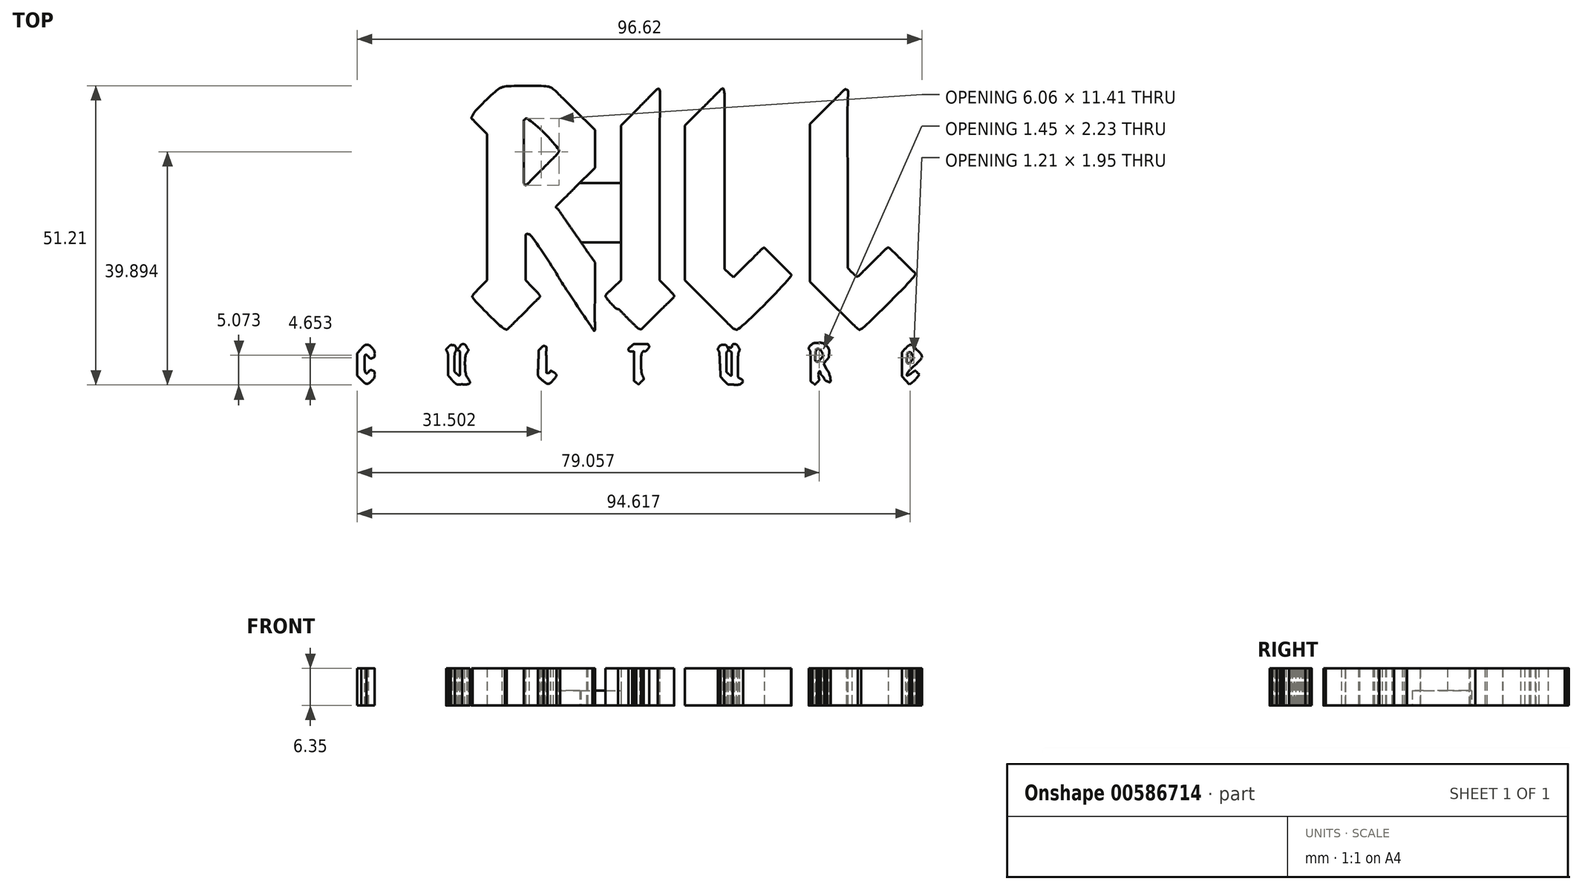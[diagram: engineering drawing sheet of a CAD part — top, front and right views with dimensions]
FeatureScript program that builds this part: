
annotation { "Feature Type Name" : "Feature", "Feature Type Description" : "" }
export const myFeature = defineFeature(function(context is Context, id is Id, definition is map)
    precondition{}
    {
        {
            var Q0;
            Q0=qCreatedBy(makeId("Top.planeOp"),FACE);
            var sketch = newSketch(context, id + "F0", { "sketchPlane" : qUnion([Q0])});
            skFitSpline(sketch, "E0", {"points": [v(-13.18, -32.43) * mm, v(-13.35, -32.29) * mm, v(-13.68, -31.93) * mm, v(-13.92, -31.65) * mm]});
            skFitSpline(sketch, "E1", {"points": [v(-13.92, -31.65) * mm, v(-14.33, -31.16) * mm, v(-14.34, -31.08) * mm, v(-14.34, -29.31) * mm]});
            skFitSpline(sketch, "E2", {"points": [v(-14.34, -29.31) * mm, v(-14.34, -28.25) * mm, v(-14.41, -27.32) * mm, v(-14.52, -27.09) * mm]});
            skFitSpline(sketch, "E3", {"points": [v(-14.52, -27.09) * mm, v(-14.68, -26.75) * mm, v(-14.65, -26.64) * mm, v(-14.33, -26.3) * mm]});
            skFitSpline(sketch, "E4", {"points": [v(-14.33, -26.3) * mm, v(-14.12, -26.08) * mm, v(-13.83, -25.93) * mm, v(-13.66, -25.96) * mm]});
            skFitSpline(sketch, "E5", {"points": [v(-13.66, -25.96) * mm, v(-13.23, -26.02) * mm, v(-12.94, -26.64) * mm, v(-13.12, -27.12) * mm]});
            skFitSpline(sketch, "E6", {"points": [v(-13.12, -27.12) * mm, v(-13.2, -27.32) * mm, v(-13.26, -28.16) * mm, v(-13.26, -29) * mm]});
            skFitSpline(sketch, "E7", {"points": [v(-13.26, -29) * mm, v(-13.26, -30.36) * mm, v(-13.23, -30.52) * mm, v(-12.9, -30.83) * mm]});
            skFitSpline(sketch, "E8", {"points": [v(-12.9, -30.83) * mm, v(-12.7, -31.01) * mm, v(-12.5, -31.16) * mm, v(-12.44, -31.16) * mm]});
            skFitSpline(sketch, "E9", {"points": [v(-12.44, -31.16) * mm, v(-12.39, -31.16) * mm, v(-12.34, -30.23) * mm, v(-12.34, -29.1) * mm]});
            skFitSpline(sketch, "E10", {"points": [v(-12.34, -29.1) * mm, v(-12.34, -27.4) * mm, v(-12.38, -27) * mm, v(-12.57, -26.89) * mm]});
            skFitSpline(sketch, "E11", {"points": [v(-12.57, -26.89) * mm, v(-12.78, -26.77) * mm, v(-12.76, -26.7) * mm, v(-12.45, -26.34) * mm]});
            skFitSpline(sketch, "E12", {"points": [v(-12.45, -26.34) * mm, v(-12, -25.81) * mm, v(-11.55, -25.81) * mm, v(-11.16, -26.35) * mm]});
            skFitSpline(sketch, "E13", {"points": [v(-11.16, -26.35) * mm, v(-10.9, -26.72) * mm, v(-10.88, -26.82) * mm, v(-11.06, -27.16) * mm]});
            skFitSpline(sketch, "E14", {"points": [v(-11.06, -27.16) * mm, v(-11.37, -27.76) * mm, v(-11.33, -30.9) * mm, v(-11, -31.58) * mm]});
            skFitSpline(sketch, "E15", {"points": [v(-11, -31.58) * mm, v(-10.63, -32.38) * mm, v(-10.84, -32.62) * mm, v(-11.97, -32.66) * mm]});
            skFitSpline(sketch, "E16", {"points": [v(-11.97, -32.66) * mm, v(-12.65, -32.7) * mm, v(-12.95, -32.63) * mm, v(-13.18, -32.43) * mm]});
            skFitSpline(sketch, "E17", {"points": [v(17.85, -32.4) * mm, v(17.47, -32.1) * mm, v(17.46, -32.1) * mm, v(17.46, -29.6) * mm]});
            skFitSpline(sketch, "E18", {"points": [v(17.46, -29.6) * mm, v(17.46, -27.09) * mm, v(17.46, -27.08) * mm, v(17.1, -27.03) * mm]});
            skFitSpline(sketch, "E19", {"points": [v(17.1, -27.03) * mm, v(16.58, -26.96) * mm, v(16.53, -26.59) * mm, v(17, -26.15) * mm]});
            skFitSpline(sketch, "E20", {"points": [v(17, -26.15) * mm, v(17.36, -25.81) * mm, v(17.54, -25.77) * mm, v(18.63, -25.77) * mm]});
            skFitSpline(sketch, "E21", {"points": [v(18.63, -25.77) * mm, v(19.58, -25.77) * mm, v(19.88, -25.83) * mm, v(19.95, -26) * mm]});
            skFitSpline(sketch, "E22", {"points": [v(19.95, -26) * mm, v(20.04, -26.25) * mm, v(19.43, -27) * mm, v(19.14, -27) * mm]});
            skFitSpline(sketch, "E23", {"points": [v(19.14, -27) * mm, v(19.04, -27) * mm, v(18.92, -27.11) * mm, v(18.87, -27.25) * mm]});
            skFitSpline(sketch, "E24", {"points": [v(18.87, -27.25) * mm, v(18.7, -27.69) * mm, v(18.77, -30.74) * mm, v(18.96, -31.27) * mm]});
            skFitSpline(sketch, "E25", {"points": [v(18.96, -31.27) * mm, v(19.13, -31.75) * mm, v(19.12, -31.82) * mm, v(18.69, -32.24) * mm]});
            skFitSpline(sketch, "E26", {"points": [v(18.69, -32.24) * mm, v(18.23, -32.7) * mm, v(18.23, -32.7) * mm, v(17.85, -32.4) * mm]});
            skLineSegment(sketch, "E27", {"start": v(-13.18, -32.43) * mm, "end": v(-13.18, -32.43) * mm});
            skFitSpline(sketch, "E28", {"points": [v(32.16, -29.32) * mm, v(32.11, -28.17) * mm, v(32.02, -27.11) * mm, v(31.95, -26.96) * mm]});
            skFitSpline(sketch, "E29", {"points": [v(31.95, -26.96) * mm, v(31.8, -26.63) * mm, v(32.38, -25.93) * mm, v(32.8, -25.93) * mm]});
            skFitSpline(sketch, "E30", {"points": [v(32.8, -25.93) * mm, v(33.14, -25.93) * mm, v(33.57, -26.74) * mm, v(33.39, -27.03) * mm]});
            skFitSpline(sketch, "E31", {"points": [v(33.39, -27.03) * mm, v(33.31, -27.14) * mm, v(33.25, -27.98) * mm, v(33.25, -28.89) * mm]});
            skFitSpline(sketch, "E32", {"points": [v(33.25, -28.89) * mm, v(33.25, -30.39) * mm, v(33.28, -30.56) * mm, v(33.59, -30.85) * mm]});
            skFitSpline(sketch, "E33", {"points": [v(33.59, -30.85) * mm, v(33.77, -31.02) * mm, v(33.98, -31.16) * mm, v(34.05, -31.16) * mm]});
            skFitSpline(sketch, "E34", {"points": [v(34.05, -31.16) * mm, v(34.12, -31.16) * mm, v(34.17, -30.27) * mm, v(34.17, -29.18) * mm]});
            skFitSpline(sketch, "E35", {"points": [v(34.17, -29.18) * mm, v(34.17, -27.6) * mm, v(34.13, -27.16) * mm, v(33.94, -27) * mm]});
            skFitSpline(sketch, "E36", {"points": [v(33.94, -27) * mm, v(33.65, -26.76) * mm, v(33.64, -26.39) * mm, v(33.93, -26.39) * mm]});
            skFitSpline(sketch, "E37", {"points": [v(33.93, -26.39) * mm, v(34.05, -26.39) * mm, v(34.18, -26.28) * mm, v(34.23, -26.16) * mm]});
            skFitSpline(sketch, "E38", {"points": [v(34.23, -26.16) * mm, v(34.37, -25.8) * mm, v(35.03, -25.88) * mm, v(35.31, -26.3) * mm]});
            skFitSpline(sketch, "E39", {"points": [v(35.31, -26.3) * mm, v(35.5, -26.6) * mm, v(35.52, -26.78) * mm, v(35.4, -27.08) * mm]});
            skFitSpline(sketch, "E40", {"points": [v(35.4, -27.08) * mm, v(35.32, -27.3) * mm, v(35.25, -28.38) * mm, v(35.25, -29.46) * mm]});
            skFitSpline(sketch, "E41", {"points": [v(35.25, -29.46) * mm, v(35.25, -31.03) * mm, v(35.3, -31.47) * mm, v(35.48, -31.63) * mm]});
            skFitSpline(sketch, "E42", {"points": [v(35.48, -31.63) * mm, v(36.1, -32.13) * mm, v(35.46, -32.7) * mm, v(34.32, -32.7) * mm]});
            skFitSpline(sketch, "E43", {"points": [v(34.32, -32.7) * mm, v(33.55, -32.68) * mm, v(33.43, -32.63) * mm, v(32.87, -32.04) * mm]});
            skLineSegment(sketch, "E44", {"start": v(32.87, -32.04) * mm, "end": v(32.25, -31.4) * mm});
            skLineSegment(sketch, "E45", {"start": v(32.25, -31.4) * mm, "end": v(32.16, -29.32) * mm});
            skFitSpline(sketch, "E46", {"points": [v(48.02, -32.41) * mm, v(47.66, -32.12) * mm, v(47.65, -32.07) * mm, v(47.65, -29.6) * mm]});
            skFitSpline(sketch, "E47", {"points": [v(47.65, -29.6) * mm, v(47.65, -28.21) * mm, v(47.6, -26.96) * mm, v(47.52, -26.81) * mm]});
            skFitSpline(sketch, "E48", {"points": [v(47.52, -26.81) * mm, v(47.35, -26.46) * mm, v(48.22, -25.62) * mm, v(48.75, -25.62) * mm]});
            skFitSpline(sketch, "E49", {"points": [v(48.75, -25.62) * mm, v(49.68, -25.62) * mm, v(50.8, -26.67) * mm, v(50.8, -27.55) * mm]});
            skFitSpline(sketch, "E50", {"points": [v(50.8, -27.55) * mm, v(50.8, -27.91) * mm, v(50.67, -28.24) * mm, v(50.35, -28.6) * mm]});
            skFitSpline(sketch, "E51", {"points": [v(50.35, -29.99) * mm, v(50.92, -31.07) * mm, v(51, -32.26) * mm, v(50.5, -32.13) * mm]});
            skFitSpline(sketch, "E52", {"points": [v(50.5, -32.13) * mm, v(50.32, -32.09) * mm, v(50.1, -31.9) * mm, v(50, -31.72) * mm]});
            skFitSpline(sketch, "E53", {"points": [v(50, -31.72) * mm, v(49.91, -31.55) * mm, v(49.75, -31.31) * mm, v(49.64, -31.2) * mm]});
            skFitSpline(sketch, "E54", {"points": [v(49.64, -31.2) * mm, v(49.54, -31.1) * mm, v(49.42, -30.93) * mm, v(49.39, -30.83) * mm]});
            skFitSpline(sketch, "E55", {"points": [v(49.39, -30.83) * mm, v(49.25, -30.41) * mm, v(49, -30.9) * mm, v(49.07, -31.43) * mm]});
            skFitSpline(sketch, "E56", {"points": [v(49.07, -31.43) * mm, v(49.13, -31.9) * mm, v(49.07, -32.07) * mm, v(48.77, -32.36) * mm]});
            skFitSpline(sketch, "E57", {"points": [v(48.77, -32.36) * mm, v(48.4, -32.71) * mm, v(48.39, -32.71) * mm, v(48.02, -32.41) * mm]});
            skLineSegment(sketch, "E58", {"start": v(50.35, -28.6) * mm, "end": v(49.89, -29.12) * mm});
            skLineSegment(sketch, "E59", {"start": v(49.89, -29.12) * mm, "end": v(50.35, -29.99) * mm});
            skFitSpline(sketch, "E60", {"points": [v(49.51, -28.16) * mm, v(49.87, -27.8) * mm, v(49.88, -27.75) * mm, v(49.66, -27.33) * mm]});
            skFitSpline(sketch, "E61", {"points": [v(49.66, -27.33) * mm, v(49.41, -26.85) * mm, v(48.81, -26.6) * mm, v(48.62, -26.9) * mm]});
            skFitSpline(sketch, "E62", {"points": [v(48.62, -26.9) * mm, v(48.56, -27) * mm, v(48.5, -27.3) * mm, v(48.5, -27.57) * mm]});
            skFitSpline(sketch, "E63", {"points": [v(48.5, -27.57) * mm, v(48.5, -28.6) * mm, v(48.85, -28.82) * mm, v(49.51, -28.16) * mm]});
            skFitSpline(sketch, "E64", {"points": [v(63.9, -26.56) * mm, v(64.24, -26.21) * mm, v(64.65, -25.93) * mm, v(64.81, -25.93) * mm]});
            skFitSpline(sketch, "E65", {"points": [v(64.81, -25.93) * mm, v(64.97, -25.93) * mm, v(65.39, -26.26) * mm, v(65.73, -26.66) * mm]});
            skFitSpline(sketch, "E66", {"points": [v(65.73, -26.66) * mm, v(66.67, -27.75) * mm, v(66.62, -28.23) * mm, v(65.44, -29.47) * mm]});
            skFitSpline(sketch, "E67", {"points": [v(65.44, -29.47) * mm, v(64.3, -30.67) * mm, v(64.17, -31.17) * mm, v(65.15, -30.6) * mm]});
            skFitSpline(sketch, "E68", {"points": [v(65.15, -30.6) * mm, v(65.58, -30.34) * mm, v(65.6, -30.34) * mm, v(65.93, -30.66) * mm]});
            skLineSegment(sketch, "E69", {"start": v(63.92, -32.01) * mm, "end": v(63.28, -31.32) * mm});
            skLineSegment(sketch, "E70", {"start": v(63.28, -31.32) * mm, "end": v(63.28, -29.26) * mm});
            skLineSegment(sketch, "E71", {"start": v(63.28, -29.26) * mm, "end": v(63.28, -27.2) * mm});
            skLineSegment(sketch, "E72", {"start": v(63.28, -27.2) * mm, "end": v(63.9, -26.56) * mm});
            skLineSegment(sketch, "E73", {"start": v(63.9, -26.56) * mm, "end": v(63.92, -32.01) * mm});
            skFitSpline(sketch, "E74", {"points": [v(65.85, -31.53) * mm, v(65.62, -31.82) * mm, v(65.24, -32.2) * mm, v(65, -32.38) * mm]});
            skLineSegment(sketch, "E75", {"start": v(65.93, -30.66) * mm, "end": v(66.26, -31) * mm});
            skLineSegment(sketch, "E76", {"start": v(66.26, -31) * mm, "end": v(65.85, -31.53) * mm});
            skFitSpline(sketch, "E77", {"points": [v(65, -28.52) * mm, v(65.3, -28.21) * mm, v(65.32, -28.15) * mm, v(65.11, -27.79) * mm]});
            skFitSpline(sketch, "E78", {"points": [v(65.11, -27.79) * mm, v(64.78, -27.2) * mm, v(64.3, -27.26) * mm, v(64.24, -27.9) * mm]});
            skFitSpline(sketch, "E79", {"points": [v(64.24, -27.9) * mm, v(64.14, -28.87) * mm, v(64.42, -29.1) * mm, v(65, -28.52) * mm]});
            skLineSegment(sketch, "E80", {"start": v(65, -32.38) * mm, "end": v(64.55, -32.7) * mm});
            skLineSegment(sketch, "E81", {"start": v(64.55, -32.7) * mm, "end": v(63.92, -32.01) * mm});
            skFitSpline(sketch, "E82", {"points": [v(-29.27, -26.64) * mm, v(-28.92, -26.25) * mm, v(-28.52, -25.93) * mm, v(-28.37, -25.93) * mm]});
            skFitSpline(sketch, "E83", {"points": [v(-28.37, -25.93) * mm, v(-27.97, -25.93) * mm, v(-26.97, -27) * mm, v(-26.97, -27.42) * mm]});
            skFitSpline(sketch, "E84", {"points": [v(-26.97, -27.42) * mm, v(-26.97, -27.94) * mm, v(-27.63, -28.23) * mm, v(-28.02, -27.88) * mm]});
            skFitSpline(sketch, "E85", {"points": [v(-28.02, -27.88) * mm, v(-28.18, -27.74) * mm, v(-28.35, -27.62) * mm, v(-28.4, -27.62) * mm]});
            skFitSpline(sketch, "E86", {"points": [v(-28.4, -27.62) * mm, v(-28.54, -27.62) * mm, v(-28.54, -30.62) * mm, v(-28.4, -30.75) * mm]});
            skFitSpline(sketch, "E87", {"points": [v(-28.4, -30.75) * mm, v(-28.35, -30.8) * mm, v(-28.18, -30.74) * mm, v(-28.02, -30.6) * mm]});
            skFitSpline(sketch, "E88", {"points": [v(-28.02, -30.6) * mm, v(-27.63, -30.25) * mm, v(-26.97, -30.54) * mm, v(-26.97, -31.05) * mm]});
            skFitSpline(sketch, "E89", {"points": [v(-26.97, -31.05) * mm, v(-26.97, -31.44) * mm, v(-28, -32.55) * mm, v(-28.35, -32.55) * mm]});
            skFitSpline(sketch, "E90", {"points": [v(-28.35, -32.55) * mm, v(-28.47, -32.55) * mm, v(-28.86, -32.24) * mm, v(-29.23, -31.85) * mm]});
            skLineSegment(sketch, "E91", {"start": v(-29.23, -31.85) * mm, "end": v(-29.9, -31.16) * mm});
            skLineSegment(sketch, "E92", {"start": v(-29.9, -31.16) * mm, "end": v(-29.9, -29.26) * mm});
            skLineSegment(sketch, "E93", {"start": v(-29.9, -29.26) * mm, "end": v(-29.9, -27.36) * mm});
            skLineSegment(sketch, "E94", {"start": v(-29.9, -27.36) * mm, "end": v(-29.27, -26.64) * mm});
            skFitSpline(sketch, "E95", {"points": [v(1.93, -32.09) * mm, v(1.13, -31.39) * mm, v(1.03, -30.98) * mm, v(1.09, -28.8) * mm]});
            skFitSpline(sketch, "E96", {"points": [v(1.09, -28.8) * mm, v(1.14, -26.93) * mm, v(1.15, -26.84) * mm, v(1.55, -26.45) * mm]});
            skFitSpline(sketch, "E97", {"points": [v(1.55, -26.45) * mm, v(1.8, -26.2) * mm, v(2.05, -26.07) * mm, v(2.2, -26.13) * mm]});
            skFitSpline(sketch, "E98", {"points": [v(2.2, -26.13) * mm, v(2.41, -26.21) * mm, v(2.45, -26.56) * mm, v(2.45, -28.46) * mm]});
            skFitSpline(sketch, "E99", {"points": [v(2.45, -28.46) * mm, v(2.45, -30.57) * mm, v(2.47, -30.7) * mm, v(2.74, -30.7) * mm]});
            skFitSpline(sketch, "E100", {"points": [v(2.74, -30.7) * mm, v(2.9, -30.7) * mm, v(3.07, -30.61) * mm, v(3.1, -30.5) * mm]});
            skFitSpline(sketch, "E101", {"points": [v(3.1, -30.5) * mm, v(3.16, -30.36) * mm, v(3.28, -30.37) * mm, v(3.6, -30.55) * mm]});
            skFitSpline(sketch, "E102", {"points": [v(3.6, -30.55) * mm, v(3.85, -30.67) * mm, v(4.07, -30.86) * mm, v(4.1, -30.96) * mm]});
            skFitSpline(sketch, "E103", {"points": [v(4.1, -30.96) * mm, v(4.18, -31.2) * mm, v(2.95, -32.55) * mm, v(2.66, -32.55) * mm]});
            skFitSpline(sketch, "E104", {"points": [v(2.66, -32.55) * mm, v(2.55, -32.55) * mm, v(2.22, -32.34) * mm, v(1.93, -32.09) * mm]});
            skLineSegment(sketch, "E105", {"start": v(-29.23, -31.85) * mm, "end": v(-29.23, -31.85) * mm});
            skFitSpline(sketch, "E106", {"points": [v(-28.7, -17.2) * mm, v(-28.52, -16.96) * mm, v(-27.75, -16.16) * mm, v(-26.98, -15.41) * mm]});
            skFitSpline(sketch, "E107", {"points": [v(-26.98, -15.41) * mm, v(-26.22, -14.67) * mm, v(-25.55, -13.9) * mm, v(-25.5, -13.72) * mm]});
            skFitSpline(sketch, "E108", {"points": [v(-25.5, -13.72) * mm, v(-25.46, -13.53) * mm, v(-25.44, -5.16) * mm, v(-25.46, 4.88) * mm]});
            skLineSegment(sketch, "E109", {"start": v(-25.03, -21.63) * mm, "end": v(-29.01, -17.64) * mm});
            skLineSegment(sketch, "E110", {"start": v(-29.01, -17.64) * mm, "end": v(-28.7, -17.2) * mm});
            skLineSegment(sketch, "E111", {"start": v(-28.7, -17.2) * mm, "end": v(-25.03, -21.63) * mm});
            skFitSpline(sketch, "E112", {"points": [v(-30.85, 23.2) * mm, v(-33.78, 23.25) * mm, v(-36.23, 23.33) * mm, v(-36.29, 23.38) * mm]});
            skFitSpline(sketch, "E113", {"points": [v(-36.29, 23.38) * mm, v(-36.35, 23.44) * mm, v(-36.33, 23.6) * mm, v(-36.26, 23.73) * mm]});
            skFitSpline(sketch, "E114", {"points": [v(-36.26, 23.73) * mm, v(-36.18, 23.86) * mm, v(-34.23, 25.88) * mm, v(-31.92, 28.2) * mm]});
            skLineSegment(sketch, "E115", {"start": v(-25.46, 4.88) * mm, "end": v(-25.5, 23.13) * mm});
            skLineSegment(sketch, "E116", {"start": v(-25.5, 23.13) * mm, "end": v(-30.85, 23.2) * mm});
            skFitSpline(sketch, "E117", {"points": [v(18.71, 32.44) * mm, v(68.6, 32.44) * mm, v(65.78, 32.49) * mm, v(65.03, 31.72) * mm]});
            skFitSpline(sketch, "E118", {"points": [v(65.03, 31.72) * mm, v(64.38, 31.05) * mm, v(58.82, 25.22) * mm, v(57.94, 24.29) * mm]});
            skLineSegment(sketch, "E119", {"start": v(-31.92, 28.2) * mm, "end": v(-27.72, 32.44) * mm});
            skLineSegment(sketch, "E120", {"start": v(-27.72, 32.44) * mm, "end": v(18.71, 32.44) * mm});
            skFitSpline(sketch, "E121", {"points": [v(-14.38, -15.65) * mm, v(-13.43, -16.62) * mm, v(-12.65, -17.47) * mm, v(-12.65, -17.55) * mm]});
            skFitSpline(sketch, "E122", {"points": [v(-12.65, -17.55) * mm, v(-12.65, -17.79) * mm, v(-20.57, -25.62) * mm, v(-20.81, -25.62) * mm]});
            skFitSpline(sketch, "E123", {"points": [v(-20.81, -25.62) * mm, v(-20.94, -25.62) * mm, v(-22.84, -23.82) * mm, v(-25.03, -21.63) * mm]});
            skLineSegment(sketch, "E124", {"start": v(57.94, 24.29) * mm, "end": v(56.98, 23.28) * mm});
            skLineSegment(sketch, "E125", {"start": v(56.98, 23.28) * mm, "end": v(20.44, 23.2) * mm});
            skLineSegment(sketch, "E126", {"start": v(20.44, 23.2) * mm, "end": v(-16.11, 23.13) * mm});
            skLineSegment(sketch, "E127", {"start": v(-16.11, 16.82) * mm, "end": v(-16.11, -1.69) * mm});
            skLineSegment(sketch, "E128", {"start": v(-16.11, 4.62) * mm, "end": v(-16.11, -13.9) * mm});
            skLineSegment(sketch, "E129", {"start": v(-16.11, -13.9) * mm, "end": v(-14.38, -15.65) * mm});
            skFitSpline(sketch, "E130", {"points": [v(-4.64, -23.2) * mm, v(-4.9, -23.1) * mm, v(-10.17, -17.75) * mm, v(-10.18, -17.57) * mm]});
            skFitSpline(sketch, "E131", {"points": [v(-10.18, -17.57) * mm, v(-10.18, -17.5) * mm, v(-9.63, -16.86) * mm, v(-8.95, -16.14) * mm]});
            skFitSpline(sketch, "E132", {"points": [v(-9.05, 11.52) * mm, v(-10.33, 12.82) * mm, v(-10.38, 12.9) * mm, v(-10.19, 13.26) * mm]});
            skFitSpline(sketch, "E133", {"points": [v(-10.19, 13.26) * mm, v(-9.88, 13.84) * mm, v(-5.65, 17.94) * mm, v(-5.18, 18.12) * mm]});
            skFitSpline(sketch, "E134", {"points": [v(-5.18, 18.12) * mm, v(-4.73, 18.29) * mm, v(2.6, 18.31) * mm, v(3.17, 18.14) * mm]});
            skFitSpline(sketch, "E135", {"points": [v(3.17, 18.14) * mm, v(3.35, 18.09) * mm, v(5.14, 16.43) * mm, v(7.14, 14.46) * mm]});
            skLineSegment(sketch, "E136", {"start": v(-8.95, -16.14) * mm, "end": v(-7.72, -14.83) * mm});
            skLineSegment(sketch, "E137", {"start": v(-7.72, -14.83) * mm, "end": v(-7.72, -2.34) * mm});
            skLineSegment(sketch, "E138", {"start": v(-7.72, -2.34) * mm, "end": v(-7.72, 10.15) * mm});
            skLineSegment(sketch, "E139", {"start": v(-7.72, 10.15) * mm, "end": v(-9.05, 11.52) * mm});
            skFitSpline(sketch, "E140", {"points": [v(7.45, 1.09) * mm, v(5.63, -0.72) * mm, v(4.14, -2.27) * mm, v(4.14, -2.35) * mm]});
            skFitSpline(sketch, "E141", {"points": [v(4.14, -2.35) * mm, v(4.14, -2.43) * mm, v(4.2, -2.51) * mm, v(4.26, -2.54) * mm]});
            skFitSpline(sketch, "E142", {"points": [v(4.26, -2.54) * mm, v(4.38, -2.6) * mm, v(4.65, -2.97) * mm, v(5.76, -4.6) * mm]});
            skFitSpline(sketch, "E143", {"points": [v(5.76, -4.6) * mm, v(6.11, -5.1) * mm, v(6.7, -5.94) * mm, v(7.05, -6.44) * mm]});
            skFitSpline(sketch, "E144", {"points": [v(7.05, -6.44) * mm, v(7.9, -7.63) * mm, v(9.1, -9.4) * mm, v(9.3, -9.73) * mm]});
            skFitSpline(sketch, "E145", {"points": [v(9.3, -9.73) * mm, v(9.39, -9.87) * mm, v(9.5, -10.02) * mm, v(9.53, -10.06) * mm]});
            skFitSpline(sketch, "E146", {"points": [v(9.53, -10.06) * mm, v(9.58, -10.1) * mm, v(9.87, -10.52) * mm, v(10.19, -10.99) * mm]});
            skLineSegment(sketch, "E147", {"start": v(7.14, 14.46) * mm, "end": v(10.76, 10.87) * mm});
            skLineSegment(sketch, "E148", {"start": v(10.76, 10.87) * mm, "end": v(10.76, 7.63) * mm});
            skLineSegment(sketch, "E149", {"start": v(10.76, 7.63) * mm, "end": v(10.76, 4.38) * mm});
            skLineSegment(sketch, "E150", {"start": v(10.76, 4.38) * mm, "end": v(7.45, 1.09) * mm});
            skFitSpline(sketch, "E151", {"points": [v(10.76, -17.3) * mm, v(10.76, -22.43) * mm, v(10.68, -23.54) * mm, v(10.34, -23.07) * mm]});
            skFitSpline(sketch, "E152", {"points": [v(10.34, -23.07) * mm, v(10.06, -22.68) * mm, v(4.97, -15.05) * mm, v(4.83, -14.81) * mm]});
            skFitSpline(sketch, "E153", {"points": [v(4.83, -14.81) * mm, v(4.24, -13.79) * mm, v(-0.42, -6.98) * mm, v(-0.54, -6.98) * mm]});
            skFitSpline(sketch, "E154", {"points": [v(-0.54, -6.98) * mm, v(-1.01, -6.98) * mm, v(-1.08, -7.55) * mm, v(-1.09, -11.2) * mm]});
            skLineSegment(sketch, "E155", {"start": v(10.19, -10.99) * mm, "end": v(10.76, -11.84) * mm});
            skLineSegment(sketch, "E156", {"start": v(10.76, -11.84) * mm, "end": v(10.76, -17.3) * mm});
            skFitSpline(sketch, "E157", {"points": [v(0.02, -16.02) * mm, v(0.64, -16.65) * mm, v(1.2, -17.28) * mm, v(1.27, -17.4) * mm]});
            skFitSpline(sketch, "E158", {"points": [v(1.27, -17.4) * mm, v(1.38, -17.6) * mm, v(0.76, -18.3) * mm, v(-1.42, -20.48) * mm]});
            skFitSpline(sketch, "E159", {"points": [v(-1.42, -20.48) * mm, v(-2.98, -22.03) * mm, v(-4.28, -23.3) * mm, v(-4.33, -23.3) * mm]});
            skFitSpline(sketch, "E160", {"points": [v(-4.33, -23.3) * mm, v(-4.37, -23.29) * mm, v(-4.5, -23.25) * mm, v(-4.64, -23.2) * mm]});
            skLineSegment(sketch, "E161", {"start": v(-1.09, -11.2) * mm, "end": v(-1.1, -14.87) * mm});
            skLineSegment(sketch, "E162", {"start": v(-1.1, -14.87) * mm, "end": v(0.02, -16.02) * mm});
            skFitSpline(sketch, "E163", {"points": [v(4.49, 7.05) * mm, v(4.6, 7.38) * mm, v(-0.85, 12.8) * mm, v(-1.18, 12.67) * mm]});
            skFitSpline(sketch, "E164", {"points": [v(-1.18, 12.67) * mm, v(-1.37, 12.6) * mm, v(-1.4, 11.76) * mm, v(-1.4, 7.14) * mm]});
            skFitSpline(sketch, "E165", {"points": [v(-1.4, 7.14) * mm, v(-1.4, 3.36) * mm, v(-1.35, 1.65) * mm, v(-1.23, 1.53) * mm]});
            skFitSpline(sketch, "E166", {"points": [v(-1.23, 1.53) * mm, v(-1.1, 1.4) * mm, v(-0.33, 2.08) * mm, v(1.67, 4.08) * mm]});
            skFitSpline(sketch, "E167", {"points": [v(1.67, 4.08) * mm, v(3.17, 5.58) * mm, v(4.44, 6.91) * mm, v(4.49, 7.05) * mm]});
            skLineSegment(sketch, "E168", {"start": v(-4.64, -23.2) * mm, "end": v(-4.64, -23.2) * mm});
            skFitSpline(sketch, "E169", {"points": [v(18.42, -23.2) * mm, v(18.27, -23.16) * mm, v(17.39, -22.37) * mm, v(16.46, -21.45) * mm]});
            skFitSpline(sketch, "E170", {"points": [v(16.46, -21.45) * mm, v(15.54, -20.52) * mm, v(14.75, -19.77) * mm, v(14.7, -19.77) * mm]});
            skFitSpline(sketch, "E171", {"points": [v(14.7, -19.77) * mm, v(14.54, -19.77) * mm, v(12.62, -17.7) * mm, v(12.61, -17.52) * mm]});
            skFitSpline(sketch, "E172", {"points": [v(12.61, -17.52) * mm, v(12.61, -17.42) * mm, v(13.2, -16.78) * mm, v(13.92, -16.1) * mm]});
            skFitSpline(sketch, "E173", {"points": [v(18.39, 14.82) * mm, v(20.13, 16.56) * mm, v(21.62, 17.94) * mm, v(21.7, 17.89) * mm]});
            skFitSpline(sketch, "E174", {"points": [v(21.7, 17.89) * mm, v(21.8, 17.83) * mm, v(21.85, 12.06) * mm, v(21.85, 1.46) * mm]});
            skLineSegment(sketch, "E175", {"start": v(13.92, -16.1) * mm, "end": v(15.23, -14.85) * mm});
            skLineSegment(sketch, "E176", {"start": v(15.23, -14.85) * mm, "end": v(15.23, -1.6) * mm});
            skLineSegment(sketch, "E177", {"start": v(15.23, -1.6) * mm, "end": v(15.23, 11.65) * mm});
            skLineSegment(sketch, "E178", {"start": v(15.23, 11.65) * mm, "end": v(18.39, 14.82) * mm});
            skFitSpline(sketch, "E179", {"points": [v(23.09, -16.14) * mm, v(23.76, -16.83) * mm, v(24.32, -17.47) * mm, v(24.32, -17.55) * mm]});
            skFitSpline(sketch, "E180", {"points": [v(24.32, -17.55) * mm, v(24.32, -17.62) * mm, v(23.05, -18.94) * mm, v(21.5, -20.47) * mm]});
            skFitSpline(sketch, "E181", {"points": [v(21.5, -20.47) * mm, v(19.52, -22.45) * mm, v(18.62, -23.24) * mm, v(18.42, -23.2) * mm]});
            skLineSegment(sketch, "E182", {"start": v(21.85, 1.46) * mm, "end": v(21.85, -14.88) * mm});
            skLineSegment(sketch, "E183", {"start": v(21.85, -14.88) * mm, "end": v(23.09, -16.14) * mm});
            skFitSpline(sketch, "E184", {"points": [v(34.64, -23.2) * mm, v(34.5, -23.15) * mm, v(32.55, -21.26) * mm, v(30.29, -19) * mm]});
            skFitSpline(sketch, "E185", {"points": [v(29.34, 14.8) * mm, v(31.1, 16.54) * mm, v(32.57, 17.97) * mm, v(32.64, 17.97) * mm]});
            skFitSpline(sketch, "E186", {"points": [v(32.64, 17.97) * mm, v(32.7, 17.97) * mm, v(32.8, 17.81) * mm, v(32.85, 17.62) * mm]});
            skFitSpline(sketch, "E187", {"points": [v(32.85, 17.62) * mm, v(32.9, 17.43) * mm, v(32.94, 10.47) * mm, v(32.94, 2.16) * mm]});
            skLineSegment(sketch, "E188", {"start": v(30.29, -19) * mm, "end": v(26.17, -14.88) * mm});
            skLineSegment(sketch, "E189", {"start": v(26.17, -14.88) * mm, "end": v(26.17, -1.62) * mm});
            skLineSegment(sketch, "E190", {"start": v(26.17, -1.62) * mm, "end": v(26.17, 11.64) * mm});
            skLineSegment(sketch, "E191", {"start": v(26.17, 11.64) * mm, "end": v(29.34, 14.8) * mm});
            skFitSpline(sketch, "E192", {"points": [v(37.03, -11.83) * mm, v(38.42, -10.43) * mm, v(39.63, -9.3) * mm, v(39.73, -9.3) * mm]});
            skFitSpline(sketch, "E193", {"points": [v(44.34, -13.87) * mm, v(44.34, -14.07) * mm, v(35.12, -23.32) * mm, v(34.94, -23.3) * mm]});
            skFitSpline(sketch, "E194", {"points": [v(34.94, -23.3) * mm, v(34.9, -23.29) * mm, v(34.76, -23.24) * mm, v(34.64, -23.2) * mm]});
            skLineSegment(sketch, "E195", {"start": v(32.94, 2.16) * mm, "end": v(32.94, -12.96) * mm});
            skLineSegment(sketch, "E196", {"start": v(32.94, -12.96) * mm, "end": v(33.72, -13.66) * mm});
            skLineSegment(sketch, "E197", {"start": v(33.72, -13.66) * mm, "end": v(34.5, -14.36) * mm});
            skLineSegment(sketch, "E198", {"start": v(34.5, -14.36) * mm, "end": v(37.03, -11.83) * mm});
            skFitSpline(sketch, "E199", {"points": [v(55.77, -23.18) * mm, v(55.67, -23.11) * mm, v(53.78, -21.27) * mm, v(51.58, -19.08) * mm]});
            skLineSegment(sketch, "E200", {"start": v(34.64, -23.2) * mm, "end": v(34.64, -23.2) * mm});
            skFitSpline(sketch, "E201", {"points": [v(50.56, 14.87) * mm, v(52.7, 17) * mm, v(53.62, 17.83) * mm, v(53.8, 17.76) * mm]});
            skFitSpline(sketch, "E202", {"points": [v(53.8, 17.76) * mm, v(54.02, 17.68) * mm, v(54.04, 16.24) * mm, v(54.04, 2.44) * mm]});
            skLineSegment(sketch, "E203", {"start": v(51.58, -19.08) * mm, "end": v(47.57, -15.1) * mm});
            skLineSegment(sketch, "E204", {"start": v(47.57, -15.1) * mm, "end": v(47.57, -1.61) * mm});
            skLineSegment(sketch, "E205", {"start": v(47.57, -1.61) * mm, "end": v(47.57, 11.89) * mm});
            skLineSegment(sketch, "E206", {"start": v(47.57, 11.89) * mm, "end": v(50.56, 14.87) * mm});
            skFitSpline(sketch, "E207", {"points": [v(54.75, -13.5) * mm, v(55.14, -13.9) * mm, v(55.53, -14.22) * mm, v(55.63, -14.22) * mm]});
            skFitSpline(sketch, "E208", {"points": [v(55.63, -14.22) * mm, v(55.72, -14.22) * mm, v(56.9, -13.11) * mm, v(58.27, -11.76) * mm]});
            skFitSpline(sketch, "E209", {"points": [v(58.27, -11.76) * mm, v(59.64, -10.4) * mm, v(60.83, -9.3) * mm, v(60.92, -9.3) * mm]});
            skFitSpline(sketch, "E210", {"points": [v(60.92, -9.3) * mm, v(61.02, -9.3) * mm, v(62.12, -10.29) * mm, v(63.36, -11.5) * mm]});
            skFitSpline(sketch, "E211", {"points": [v(63.36, -11.5) * mm, v(65.36, -13.45) * mm, v(65.61, -13.74) * mm, v(65.47, -14.01) * mm]});
            skFitSpline(sketch, "E212", {"points": [v(65.47, -14.01) * mm, v(65.3, -14.31) * mm, v(56.7, -22.94) * mm, v(56.31, -23.18) * mm]});
            skFitSpline(sketch, "E213", {"points": [v(56.31, -23.18) * mm, v(56.07, -23.33) * mm, v(56.02, -23.33) * mm, v(55.77, -23.18) * mm]});
            skLineSegment(sketch, "E214", {"start": v(54.04, 2.44) * mm, "end": v(54.04, -12.78) * mm});
            skLineSegment(sketch, "E215", {"start": v(54.04, -12.78) * mm, "end": v(54.75, -13.5) * mm});
            skLineSegment(sketch, "E216", {"start": v(55.77, -23.18) * mm, "end": v(55.77, -23.18) * mm});
            skLineSegment(sketch, "E217.left", {"start": v(-16.11, 1.8) * mm, "end": v(-16.11, -8.36) * mm});
            skLineSegment(sketch, "E217.right", {"start": v(47.57, 1.8) * mm, "end": v(47.57, -8.36) * mm});
            skLineSegment(sketch, "E218", {"start": v(-16.11, 16.82) * mm, "end": v(-16.11, 23.13) * mm});
            skLineSegment(sketch, "E219", {"start": v(39.73, -9.3) * mm, "end": v(44.34, -13.87) * mm});
            skLineSegment(sketch, "E220", {"start": v(-16.11, 1.8) * mm, "end": v(-7.72, 1.8) * mm});
            skLineSegment(sketch, "E221", {"start": v(8.17, 1.8) * mm, "end": v(15.23, 1.8) * mm});
            skLineSegment(sketch, "E222", {"start": v(21.85, 1.8) * mm, "end": v(26.17, 1.8) * mm});
            skLineSegment(sketch, "E223", {"start": v(32.94, 1.8) * mm, "end": v(47.57, 1.8) * mm});
            skLineSegment(sketch, "E224", {"start": v(-16.11, -8.36) * mm, "end": v(-7.72, -8.36) * mm});
            skLineSegment(sketch, "E225", {"start": v(-1.04, -8.36) * mm, "end": v(0.48, -8.36) * mm});
            skLineSegment(sketch, "E226", {"start": v(8.38, -8.36) * mm, "end": v(15.23, -8.36) * mm});
            skLineSegment(sketch, "E227", {"start": v(21.85, -8.36) * mm, "end": v(26.17, -8.36) * mm});
            skLineSegment(sketch, "E228", {"start": v(32.94, -8.36) * mm, "end": v(47.57, -8.36) * mm});
            skSolve(sketch);
        }
        {
            var Q0;
            Q0=makeQuery(id+"F0.imprint","IMPRINT",FACE,{"disambiguationData":[TD([[makeQuery(id+"F0.imprint","IMPRINT",EDGE,{"derivedFrom":sQuery(id+"F0.wireOp",EDGE,"E106")}),-1.0]])]});
            var Q1;
            Q1=makeQuery(id+"F0.imprint","IMPRINT",FACE,{"disambiguationData":[TD([[makeQuery(id+"F0.imprint","IMPRINT",EDGE,{"derivedFrom":sQuery(id+"F0.wireOp",EDGE,"E130")}),-1.0]])]});
            var Q2;
            Q2=makeQuery(id+"F0.imprint","IMPRINT",FACE,{"disambiguationData":[TD([[makeQuery(id+"F0.imprint","IMPRINT",EDGE,{"derivedFrom":sQuery(id+"F0.wireOp",EDGE,"E169")}),-1.0]])]});
            var Q3;
            Q3=makeQuery(id+"F0.imprint","IMPRINT",FACE,{"disambiguationData":[TD([[makeQuery(id+"F0.imprint","IMPRINT",EDGE,{"derivedFrom":sQuery(id+"F0.wireOp",EDGE,"E184")}),-1.0]])]});
            var Q4;
            Q4=makeQuery(id+"F0.imprint","IMPRINT",FACE,{"disambiguationData":[TD([[makeQuery(id+"F0.imprint","IMPRINT",EDGE,{"derivedFrom":sQuery(id+"F0.wireOp",EDGE,"E199")}),-1.0]])]});
            extrude(context, id + "F1", {"entities" : qUnion([Q0, Q1, Q2, Q3, Q4]), "depth" : 6.35 * mm, "offsetDistance" : 25.4 * mm});
        }
        {
            var Q0;
            Q0=makeQuery(id+"F0.imprint","IMPRINT",FACE,{"disambiguationData":[TD([[makeQuery(id+"F0.imprint","IMPRINT",EDGE,{"derivedFrom":sQuery(id+"F0.wireOp",EDGE,"E82")}),-1.0]])]});
            var Q1;
            Q1=makeQuery(id+"F0.imprint","IMPRINT",FACE,{"disambiguationData":[TD([[makeQuery(id+"F0.imprint","IMPRINT",EDGE,{"derivedFrom":sQuery(id+"F0.wireOp",EDGE,"E0")}),-1.0]])]});
            var Q2;
            Q2=makeQuery(id+"F0.imprint","IMPRINT",FACE,{"disambiguationData":[TD([[makeQuery(id+"F0.imprint","IMPRINT",EDGE,{"derivedFrom":sQuery(id+"F0.wireOp",EDGE,"E95")}),-1.0]])]});
            var Q3;
            Q3=makeQuery(id+"F0.imprint","IMPRINT",FACE,{"disambiguationData":[TD([[makeQuery(id+"F0.imprint","IMPRINT",EDGE,{"derivedFrom":sQuery(id+"F0.wireOp",EDGE,"E17")}),-1.0]])]});
            var Q4;
            Q4=makeQuery(id+"F0.imprint","IMPRINT",FACE,{"disambiguationData":[TD([[makeQuery(id+"F0.imprint","IMPRINT",EDGE,{"derivedFrom":sQuery(id+"F0.wireOp",EDGE,"E46")}),-1.0]])]});
            var Q5;
            Q5=makeQuery(id+"F0.imprint","IMPRINT",FACE,{"disambiguationData":[TD([[makeQuery(id+"F0.imprint","IMPRINT",EDGE,{"derivedFrom":sQuery(id+"F0.wireOp",EDGE,"E28")}),-1.0]])]});
            var Q6;
            Q6=makeQuery(id+"F0.imprint","IMPRINT",FACE,{"disambiguationData":[TD([[makeQuery(id+"F0.imprint","IMPRINT",EDGE,{"derivedFrom":sQuery(id+"F0.wireOp",EDGE,"E64")}),-1.0]])]});
            var Q7;
            Q7=makeQuery(id+"F0.imprint","IMPRINT",FACE,{"disambiguationData":[TD([[makeQuery(id+"F0.imprint","IMPRINT",EDGE,{"derivedFrom":sQuery(id+"F0.wireOp",EDGE,"E69")}),-1.0]])]});
            extrude(context, id + "F2", {"entities" : qUnion([Q0, Q1, Q2, Q3, Q4, Q5, Q6, Q7]), "depth" : 6.35 * mm, "offsetDistance" : 25.4 * mm});
        }
        {
            var Q0;
            {var subQ0=sQuery(id+"F0.wireOp",EDGE,"E217.left");Q0=makeQuery(id+"F0.imprint","IMPRINT",FACE,{"disambiguationData":[TD([[makeQuery(id+"F0.imprint","IMPRINT",EDGE,{"derivedFrom":subQ0}),1.0]])]});}
            var Q1;
            Q1=makeQuery(id+"F0.imprint","IMPRINT",FACE,{"disambiguationData":[TD([[makeQuery(id+"F0.imprint","IMPRINT",EDGE,{"derivedFrom":sQuery(id+"F0.wireOp",EDGE,"E140")}),1.0]])]});
            var Q2;
            {var subQ5=sQuery(id+"F0.wireOp",EDGE,"E182");var subQ6=sQuery(id+"F0.wireOp",EDGE,"E174");var subQ7=makeQuery(id+"F0.imprint","INTERSECT",VERTEX,{"derivedFrom":[subQ6,subQ5]});Q2=makeQuery(id+"F0.imprint","IMPRINT",FACE,{"disambiguationData":[TD([[makeQuery(id+"F0.imprint","IMPRINT",EDGE,{"disambiguationData":[TD([[subQ7,1.0]])],"derivedFrom":subQ6}),1.0]])]});}
            var Q3;
            {var subQ0=sQuery(id+"F0.wireOp",EDGE,"E217.right");Q3=makeQuery(id+"F0.imprint","IMPRINT",FACE,{"disambiguationData":[TD([[makeQuery(id+"F0.imprint","IMPRINT",EDGE,{"derivedFrom":subQ0}),-1.0]])]});}
            extrude(context, id + "F3", {"entities" : qUnion([Q0, Q1, Q2, Q3]), "depth" : 2.54 * mm, "offsetDistance" : 25.4 * mm});
        }
        {
            var Q0;
            Q0=makeQuery(id+"F0.imprint","IMPRINT",FACE,{"disambiguationData":[TD([[makeQuery(id+"F0.imprint","IMPRINT",EDGE,{"derivedFrom":sQuery(id+"F0.wireOp",EDGE,"E132")}),-1.0]])]});
            var Q1;
            Q1=makeQuery(id+"F0.imprint","IMPRINT",FACE,{"disambiguationData":[TD([[makeQuery(id+"F0.imprint","IMPRINT",EDGE,{"derivedFrom":sQuery(id+"F0.wireOp",EDGE,"E140")}),-1.0]])]});
            var Q2;
            {var subQ5=sQuery(id+"F0.wireOp",EDGE,"E173");Q2=makeQuery(id+"F0.imprint","IMPRINT",FACE,{"disambiguationData":[TD([[makeQuery(id+"F0.imprint","IMPRINT",EDGE,{"derivedFrom":subQ5}),-1.0]])]});}
            var Q3;
            {var subQ7=sQuery(id+"F0.wireOp",EDGE,"E182");var subQ8=sQuery(id+"F0.wireOp",EDGE,"E174");var subQ9=makeQuery(id+"F0.imprint","INTERSECT",VERTEX,{"derivedFrom":[subQ8,subQ7]});Q3=makeQuery(id+"F0.imprint","IMPRINT",FACE,{"disambiguationData":[TD([[makeQuery(id+"F0.imprint","IMPRINT",EDGE,{"disambiguationData":[TD([[subQ9,1.0]])],"derivedFrom":subQ8}),-1.0]])]});}
            var Q4;
            {var subQ0=sQuery(id+"F0.wireOp",EDGE,"E195");var subQ1=sQuery(id+"F0.wireOp",EDGE,"E187");var subQ2=makeQuery(id+"F0.imprint","INTERSECT",VERTEX,{"derivedFrom":[subQ1,subQ0]});Q4=makeQuery(id+"F0.imprint","IMPRINT",FACE,{"disambiguationData":[TD([[makeQuery(id+"F0.imprint","IMPRINT",EDGE,{"disambiguationData":[TD([[subQ2,1.0]])],"derivedFrom":subQ1}),-1.0]])]});}
            var Q5;
            Q5=makeQuery(id+"F0.imprint","IMPRINT",FACE,{"disambiguationData":[TD([[makeQuery(id+"F0.imprint","IMPRINT",EDGE,{"derivedFrom":sQuery(id+"F0.wireOp",EDGE,"E185")}),-1.0]])]});
            extrude(context, id + "F4", {"entities" : qUnion([Q0, Q1, Q2, Q3, Q4, Q5]), "depth" : 6.35 * mm, "offsetDistance" : 25.4 * mm});
        }
        {
            var Q0;
            {var subQ5=sQuery(id+"F0.wireOp",EDGE,"E145");Q0=makeQuery(id+"F0.imprint","IMPRINT",FACE,{"disambiguationData":[TD([[makeQuery(id+"F0.imprint","IMPRINT",EDGE,{"derivedFrom":subQ5}),-1.0]])]});}
            extrude(context, id + "F5", {"entities" : qUnion([Q0]), "operationType" : NewBodyOperationType.ADD, "depth" : 6.35 * mm, "offsetDistance" : 25.4 * mm});
        }
        {
            var Q0;
            {var subQ5=sQuery(id+"F0.wireOp",EDGE,"E190");var subQ7=sQuery(id+"F0.wireOp",EDGE,"E189");var subQ8=makeQuery(id+"F0.imprint","INTERSECT",VERTEX,{"derivedFrom":[subQ7,subQ5]});Q0=makeQuery(id+"F0.imprint","IMPRINT",FACE,{"disambiguationData":[TD([[makeQuery(id+"F0.imprint","IMPRINT",EDGE,{"disambiguationData":[TD([[subQ8,1.0]])],"derivedFrom":subQ7}),-1.0]])]});}
            extrude(context, id + "F6", {"entities" : qUnion([Q0]), "depth" : 6.35 * mm, "offsetDistance" : 25.4 * mm});
        }
    });
